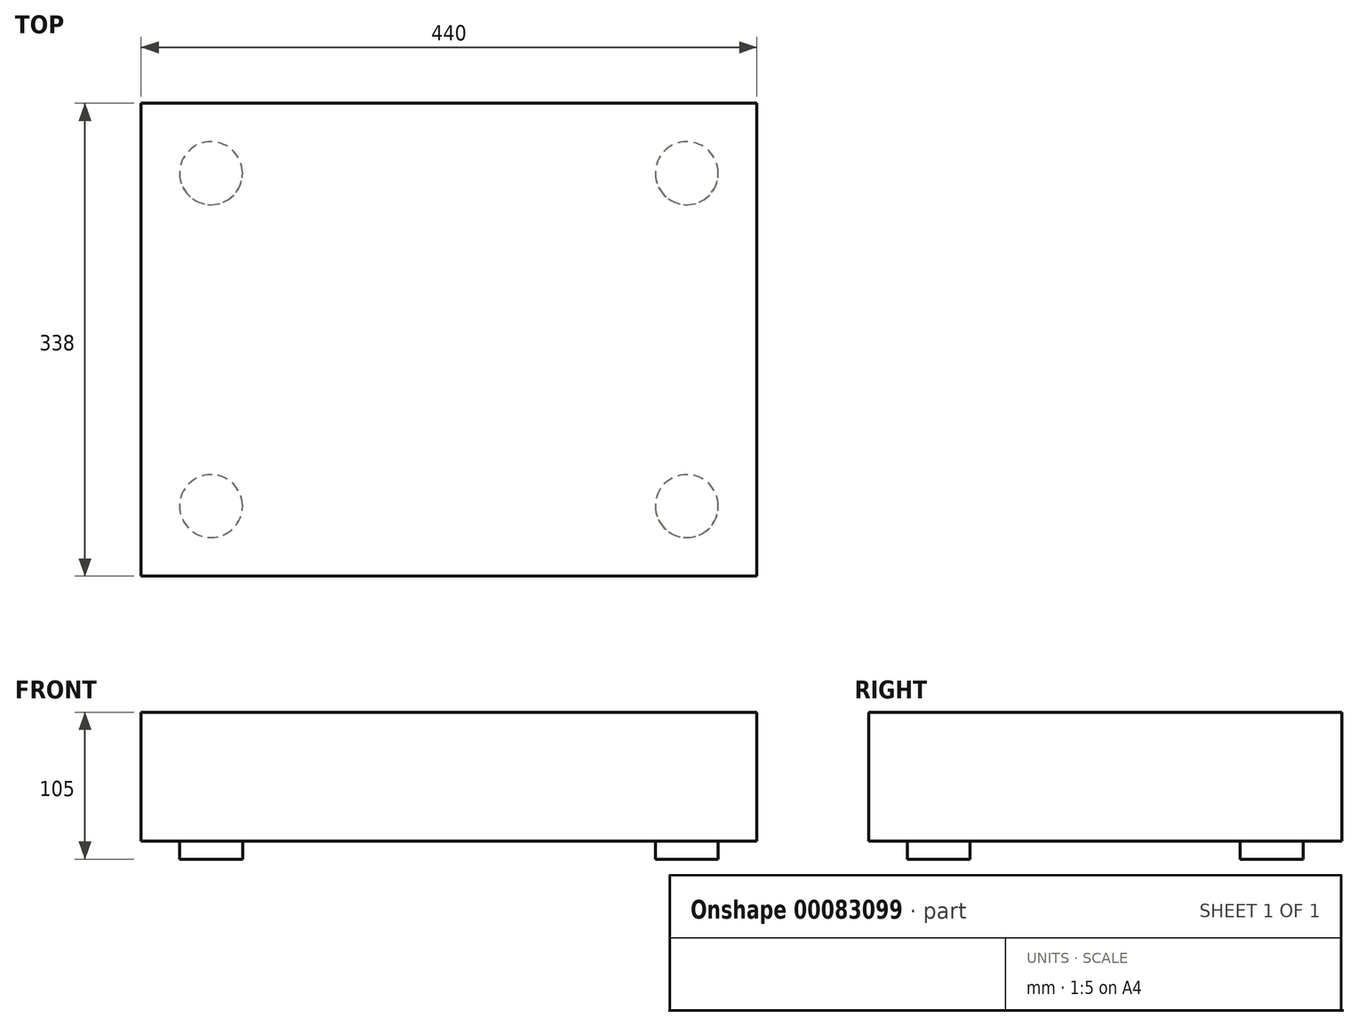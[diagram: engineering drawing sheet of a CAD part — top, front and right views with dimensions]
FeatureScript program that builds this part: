
annotation { "Feature Type Name" : "Feature", "Feature Type Description" : "" }
export const myFeature = defineFeature(function(context is Context, id is Id, definition is map)
    precondition{}
    {
        {
            var Q0;
            Q0=qCreatedBy(makeId("Top.planeOp"),FACE);
            var sketch = newSketch(context, id + "F0", { "sketchPlane" : qUnion([Q0])});
            skLineSegment(sketch, "E0.bottom", {"start": v(0, 0) * mm, "end": v(440, 0) * mm});
            skLineSegment(sketch, "E0.top", {"start": v(0, 338) * mm, "end": v(440, 338) * mm});
            skLineSegment(sketch, "E0.left", {"start": v(0, 0) * mm, "end": v(0, 338) * mm});
            skLineSegment(sketch, "E0.right", {"start": v(440, 0) * mm, "end": v(440, 338) * mm});
            skSolve(sketch);
        }
        {
            var Q0;
            Q0 = qSketchRegion(id + "F0", true);
            extrude(context, id + "F1", {"entities" : qUnion([Q0]), "depth" : (105 - 13) * mm});
        }
        {
            var Q0;
            Q0=makeQuery(id+"F1.opExtrude","CAP_FACE",FACE,{"disambiguationData":[OSD([sQuery(id+"F0.wireOp",EDGE,"E0.bottom"),sQuery(id+"F0.wireOp",EDGE,"E0.top"),sQuery(id+"F0.wireOp",EDGE,"E0.left"),sQuery(id+"F0.wireOp",EDGE,"E0.right")])],"isStart":true});
            var sketch = newSketch(context, id + "F2", { "sketchPlane" : qUnion([Q0])});
            skCircle(sketch, "E1", {"center": v(50, -50) * mm, "radius": 22.5 * mm});
            skCircle(sketch, "E2.0.1.0", {"center": v(50, -288) * mm, "radius": 22.5 * mm});
            skCircle(sketch, "E2.1.0.0", {"center": v(390, -50) * mm, "radius": 22.5 * mm});
            skCircle(sketch, "E2.1.1.0", {"center": v(390, -288) * mm, "radius": 22.5 * mm});
            skLineSegment(sketch, "E2.direction1", {"start": v(50, -50) * mm, "end": v(390, -50) * mm, "construction": true});
            skLineSegment(sketch, "E2.direction2", {"start": v(50, -50) * mm, "end": v(50, -288) * mm, "construction": true});
            skSolve(sketch);
        }
        {
            var Q0;
            Q0=makeQuery(id+"F2.imprint","IMPRINT",FACE,{"disambiguationData":[TD([[makeQuery(id+"F2.imprint","IMPRINT",EDGE,{"derivedFrom":sQuery(id+"F2.wireOp",EDGE,"E1")}),1.0]])]});
            var Q1;
            Q1=makeQuery(id+"F2.imprint","IMPRINT",FACE,{"disambiguationData":[TD([[makeQuery(id+"F2.imprint","IMPRINT",EDGE,{"derivedFrom":sQuery(id+"F2.wireOp",EDGE,"E2.1.0.0")}),1.0]])]});
            var Q2;
            Q2=makeQuery(id+"F2.imprint","IMPRINT",FACE,{"disambiguationData":[TD([[makeQuery(id+"F2.imprint","IMPRINT",EDGE,{"derivedFrom":sQuery(id+"F2.wireOp",EDGE,"E2.1.1.0")}),1.0]])]});
            var Q3;
            Q3=makeQuery(id+"F2.imprint","IMPRINT",FACE,{"disambiguationData":[TD([[makeQuery(id+"F2.imprint","IMPRINT",EDGE,{"derivedFrom":sQuery(id+"F2.wireOp",EDGE,"E2.0.1.0")}),1.0]])]});
            extrude(context, id + "F3", {"entities" : qUnion([Q0, Q1, Q2, Q3]), "operationType" : NewBodyOperationType.ADD, "depth" : 13 * mm});
        }
    });
